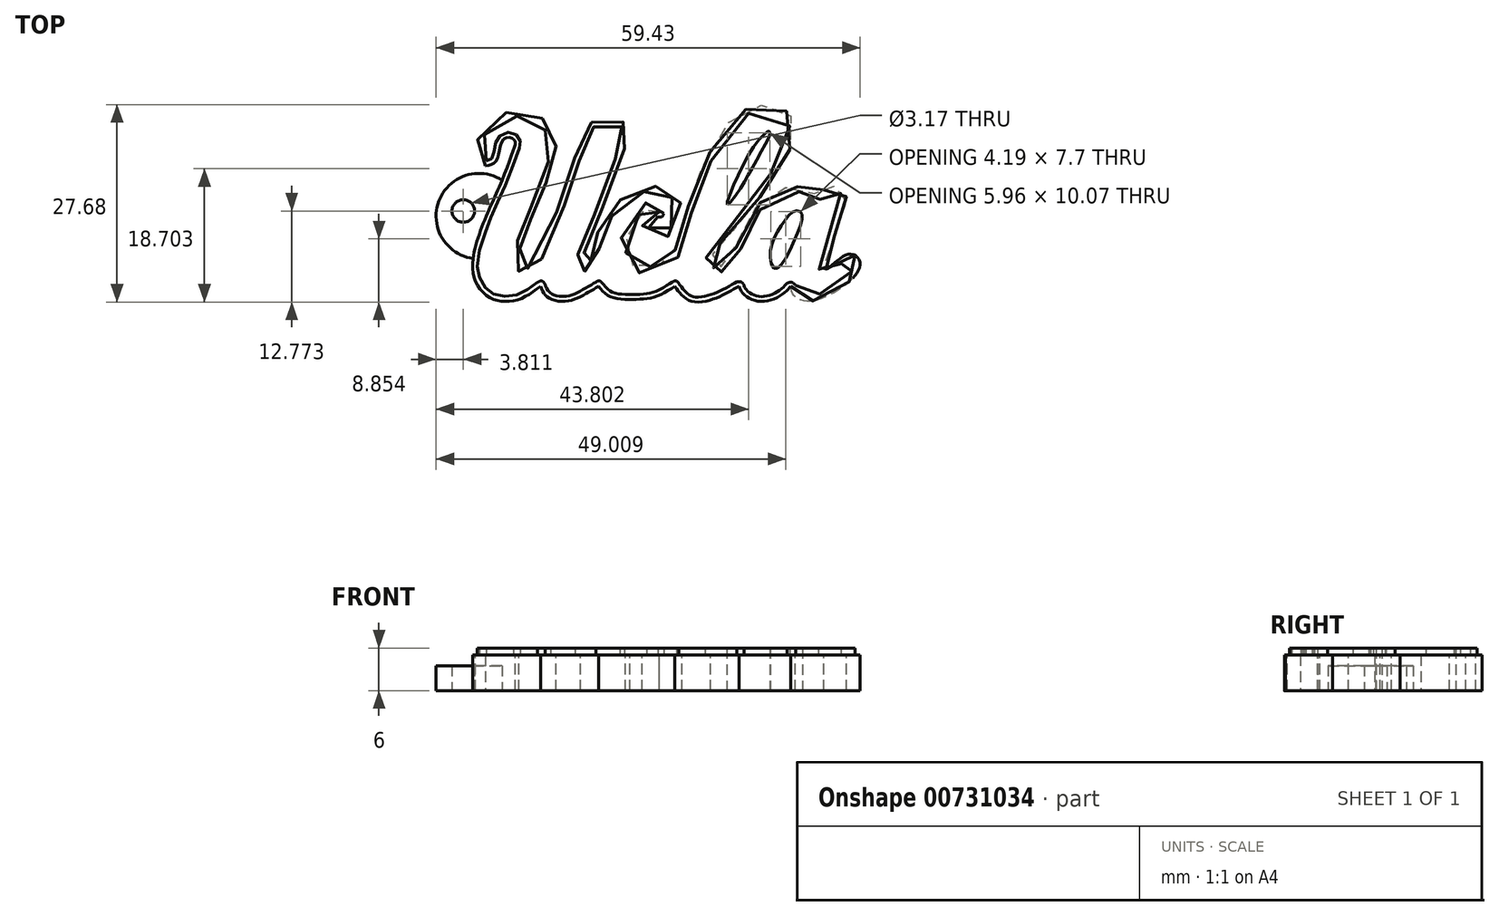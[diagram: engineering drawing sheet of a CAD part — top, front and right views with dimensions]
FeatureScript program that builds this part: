
annotation { "Feature Type Name" : "Feature", "Feature Type Description" : "" }
export const myFeature = defineFeature(function(context is Context, id is Id, definition is map)
    precondition{}
    {
        {
            var Q0;
            Q0=qCreatedBy(makeId("Top.planeOp"),FACE);
            var sketch = newSketch(context, id + "F0", { "sketchPlane" : qUnion([Q0])});
            skFitSpline(sketch, "E0", {"points": [v(-32.29, -2.1) * mm, v(-33.49, -1.15) * mm, v(-33.6, 0.71) * mm, v(-32.2, 3.77) * mm, v(-29.25, 5.4) * mm, v(-25.96, 5.38) * mm, v(-24.08, 4.39) * mm, v(-22.9, 2.53) * mm, v(-22.38, 0.67) * mm, v(-22.7, -1.4) * mm, v(-23.94, -4.94) * mm, v(-25.28, -8.23) * mm, v(-26.3, -10.38) * mm, v(-27.03, -12.53) * mm, v(-27.5, -13.99) * mm, v(-27.48, -15.85) * mm, v(-26.87, -16.53) * mm, v(-25.96, -16.2) * mm, v(-21.88, -7.39) * mm, v(-19.93, -1.51) * mm, v(-18.07, 3.2) * mm, v(-17.5, 3.93) * mm, v(-15.96, 4.16) * mm, v(-13.44, 4.16) * mm, v(-12.3, 3.64) * mm, v(-12.06, 2.82) * mm, v(-13.21, -0.8) * mm, v(-16.07, -8.52) * mm, v(-18.02, -13.37) * mm, v(-18.93, -15.64) * mm, v(-18.77, -16.2) * mm, v(-17.68, -15.6) * mm, v(-17.18, -14.6) * mm, v(-16.89, -12.63) * mm, v(-16.18, -10.6) * mm, v(-14.53, -7.95) * mm, v(-11.2, -5.41) * mm, v(-8.81, -4.94) * mm, v(-6.57, -5.32) * mm, v(-5.2, -6.7) * mm, v(-4.78, -8.93) * mm, v(-6.25, -11.76) * mm, v(-8.72, -12.13) * mm, v(-10, -11.15) * mm, v(-10.29, -9.56) * mm, v(-9.4, -8.47) * mm, v(-7.95, -8.57) * mm], "startDerivative": vector(-82.8, 46.2) * mm, "endDerivative": vector(90.83, -22.48) * mm});
            skFitSpline(sketch, "E1", {"points": [v(-7.95, -8.57) * mm, v(-7.95, -8.11) * mm, v(-8.83, -7.77) * mm, v(-10.4, -8.57) * mm, v(-11.92, -10.56) * mm, v(-12.67, -13.71) * mm, v(-12.03, -15.69) * mm, v(-10.74, -16.35) * mm, v(-8.52, -16.16) * mm, v(-6.7, -15.46) * mm, v(-5.84, -14.33) * mm, v(-5.27, -12.22) * mm, v(-3.9, -7.93) * mm, v(-2.26, -3.3) * mm, v(1.46, 3.6) * mm, v(4.6, 5.97) * mm, v(8.02, 6.43) * mm, v(10.24, 5.25) * mm, v(11.12, 2.73) * mm, v(10.04, -0.56) * mm, v(7.34, -4.94) * mm, v(2.14, -11.45) * mm, v(0, -13.65) * mm, v(-0.6, -14.96) * mm, v(-0.58, -16.28) * mm, v(0.49, -16.35) * mm, v(2.44, -15.42) * mm, v(2.96, -12.87) * mm, v(5.1, -8.57) * mm, v(8.24, -5.64) * mm, v(10.53, -5.05) * mm, v(13.28, -5.46) * mm, v(14.14, -6.2) * mm, v(15.12, -5.5) * mm, v(16.75, -4.98) * mm, v(18.02, -5.48) * mm, v(18.31, -6.68) * mm, v(17.9, -8.57) * mm, v(16.48, -12.2) * mm, v(15.23, -15.48) * mm, v(15.28, -16.55) * mm, v(16.48, -15.9) * mm, v(18.43, -14.55) * mm, v(19.83, -14.85) * mm, v(20.22, -16.14) * mm, v(19.18, -17.86) * mm, v(17.54, -19.27) * mm, v(14.4, -20.86) * mm, v(12.05, -20.97) * mm, v(10.88, -20.13) * mm, v(10.53, -19) * mm], "startDerivative": vector(14.19, 54.27) * mm, "endDerivative": vector(-13.26, 84.42) * mm});
            skFitSpline(sketch, "E2", {"points": [v(10.53, -19) * mm, v(9.7, -19.84) * mm, v(7.52, -20.97) * mm, v(5.05, -20.84) * mm, v(3.6, -19.7) * mm, v(3.28, -19) * mm], "startDerivative": vector(-4.2, -4.82) * mm, "endDerivative": vector(-1.54, 4.94) * mm});
            skFitSpline(sketch, "E3", {"points": [v(3.28, -19) * mm, v(1.6, -19.9) * mm, v(-0.58, -20.86) * mm, v(-3.23, -21.13) * mm, v(-4.78, -20.2) * mm, v(-5.73, -19) * mm], "startDerivative": vector(-8.47, -4.65) * mm, "endDerivative": vector(-5.03, 7.1) * mm});
            skFitSpline(sketch, "E4", {"points": [v(-5.73, -19) * mm, v(-8.74, -20.54) * mm, v(-11.67, -20.81) * mm, v(-14.7, -20.47) * mm, v(-16.43, -19) * mm], "startDerivative": vector(-11.13, -6.91) * mm, "endDerivative": vector(-6.78, 7.91) * mm});
            skFitSpline(sketch, "E5", {"points": [v(-16.43, -19) * mm, v(-18.52, -20.2) * mm, v(-21.15, -21.1) * mm, v(-23.7, -20.4) * mm, v(-24.55, -19) * mm], "startDerivative": vector(-7.97, -4.77) * mm, "endDerivative": vector(-2.84, 7.32) * mm});
            skFitSpline(sketch, "E6", {"points": [v(-24.55, -19) * mm, v(-27.1, -20.63) * mm, v(-29.57, -21.1) * mm, v(-31.9, -20.43) * mm, v(-33.67, -18.25) * mm, v(-34, -15.1) * mm, v(-32.24, -9.36) * mm, v(-29.94, -4.1) * mm, v(-28.27, 0.33) * mm, v(-28.1, 1.28) * mm, v(-28.73, 1.87) * mm, v(-29.86, 1.5) * mm, v(-30.45, -0.67) * mm, v(-31.18, -1.8) * mm, v(-32.29, -2.1) * mm], "startDerivative": vector(-31.72, -23.82) * mm, "endDerivative": vector(-24.62, -3.1) * mm});
            skFitSpline(sketch, "E7", {"points": [v(1.64, -7.53) * mm, v(2.2, -5.58) * mm, v(5.1, 0.21) * mm, v(7.17, 2.65) * mm, v(7.51, 2.77) * mm, v(7.6, 2.43) * mm, v(7.15, 1.33) * mm, v(5, -2.55) * mm, v(3.3, -5.52) * mm, v(1.64, -7.53) * mm]});
            skFitSpline(sketch, "E8", {"points": [v(11.84, -8.5) * mm, v(10.91, -8.5) * mm, v(9.6, -9.9) * mm, v(8.17, -12.27) * mm, v(7.65, -15.1) * mm, v(8.34, -16.53) * mm, v(9.82, -15.06) * mm, v(11.05, -12.48) * mm, v(12.15, -9.46) * mm, v(11.84, -8.5) * mm]});
            skArc(sketch, "E9", {"start": v(-29.94, -4.1) * mm, "mid": v(-38.81, -7.08) * mm, "end": v(-34, -15.1) * mm});
            skCircle(sketch, "E10", {"center": v(-35.37, -8.43) * mm, "radius": 1.59 * mm});
            skFitSpline(sketch, "E11.0", {"points": [v(-31.95, -1.49) * mm, v(-32.05, -1.43) * mm, v(-32.26, -1.31) * mm, v(-32.53, -1.15) * mm, v(-32.73, -1) * mm, v(-32.86, -0.85) * mm, v(-32.93, -0.72) * mm, v(-32.99, -0.53) * mm, v(-33.01, -0.27) * mm, v(-33, 0.06) * mm, v(-32.95, 0.44) * mm, v(-32.83, 1) * mm, v(-32.6, 1.76) * mm, v(-32.26, 2.49) * mm, v(-31.92, 3) * mm, v(-31.64, 3.36) * mm, v(-31.33, 3.66) * mm, v(-30.87, 4.03) * mm, v(-30.21, 4.4) * mm, v(-29.32, 4.7) * mm, v(-28.37, 4.86) * mm, v(-27.4, 4.9) * mm, v(-26.64, 4.81) * mm, v(-26.1, 4.7) * mm, v(-25.6, 4.56) * mm, v(-25.2, 4.37) * mm, v(-24.85, 4.14) * mm, v(-24.6, 3.93) * mm, v(-24.38, 3.7) * mm, v(-24.1, 3.32) * mm, v(-23.84, 2.88) * mm, v(-23.61, 2.42) * mm, v(-23.4, 1.94) * mm, v(-23.2, 1.38) * mm, v(-23.09, 0.85) * mm, v(-23.06, 0.46) * mm, v(-23.08, 0.04) * mm, v(-23.15, -0.41) * mm, v(-23.29, -0.93) * mm, v(-23.45, -1.5) * mm, v(-23.82, -2.61) * mm, v(-24.35, -4.04) * mm, v(-24.88, -5.45) * mm, v(-25.28, -6.46) * mm, v(-25.6, -7.24) * mm, v(-25.86, -7.8) * mm, v(-26.1, -8.34) * mm, v(-26.43, -8.98) * mm, v(-26.75, -9.63) * mm, v(-26.98, -10.2) * mm, v(-27.2, -10.77) * mm, v(-27.38, -11.34) * mm, v(-27.54, -11.87) * mm, v(-27.66, -12.24) * mm, v(-27.78, -12.55) * mm, v(-27.94, -12.98) * mm, v(-28.1, -13.44) * mm, v(-28.22, -13.99) * mm, v(-28.28, -14.44) * mm, v(-28.31, -14.9) * mm, v(-28.3, -15.37) * mm, v(-28.22, -15.84) * mm, v(-28.07, -16.3) * mm, v(-27.82, -16.7) * mm, v(-27.55, -16.95) * mm, v(-27.3, -17.1) * mm, v(-27.1, -17.2) * mm, v(-26.87, -17.26) * mm, v(-26.62, -17.28) * mm, v(-26.35, -17.25) * mm, v(-26, -17.14) * mm, v(-25.63, -16.9) * mm, v(-25.24, -16.47) * mm, v(-24.87, -15.93) * mm, v(-24.48, -15.29) * mm, v(-23.96, -14.3) * mm, v(-23.28, -12.85) * mm, v(-22.48, -10.95) * mm, v(-21.85, -9.35) * mm, v(-21.4, -8.14) * mm, v(-21, -7.02) * mm, v(-20.58, -5.78) * mm, v(-20.16, -4.48) * mm, v(-19.85, -3.48) * mm, v(-19.59, -2.68) * mm, v(-19.38, -2.07) * mm, v(-19.16, -1.44) * mm, v(-18.84, -0.56) * mm, v(-18.42, 0.55) * mm, v(-18.01, 1.58) * mm, v(-17.72, 2.27) * mm, v(-17.52, 2.71) * mm, v(-17.36, 3.06) * mm, v(-17.27, 3.22) * mm, v(-17.23, 3.27) * mm, v(-17.22, 3.29) * mm, v(-17.22, 3.3) * mm, v(-17.2, 3.3) * mm, v(-17.1, 3.34) * mm, v(-16.85, 3.39) * mm, v(-16.52, 3.42) * mm, v(-16.13, 3.45) * mm, v(-15.69, 3.47) * mm, v(-15.24, 3.5) * mm, v(-14.79, 3.52) * mm, v(-14.35, 3.53) * mm, v(-13.95, 3.52) * mm, v(-13.6, 3.48) * mm, v(-13.31, 3.42) * mm, v(-13.08, 3.34) * mm, v(-12.92, 3.25) * mm, v(-12.83, 3.18) * mm, v(-12.8, 3.14) * mm, v(-12.78, 3.11) * mm, v(-12.77, 3.08) * mm, v(-12.75, 2.97) * mm, v(-12.76, 2.75) * mm, v(-12.82, 2.42) * mm, v(-12.97, 1.87) * mm, v(-13.27, 1.01) * mm, v(-13.74, -0.23) * mm, v(-14.27, -1.64) * mm, v(-14.83, -3.14) * mm, v(-15.4, -4.7) * mm, v(-15.98, -6.27) * mm, v(-16.54, -7.78) * mm, v(-17.06, -9.18) * mm, v(-17.55, -10.45) * mm, v(-18.02, -11.61) * mm, v(-18.39, -12.49) * mm, v(-18.68, -13.13) * mm, v(-18.9, -13.6) * mm, v(-19.1, -14.05) * mm, v(-19.3, -14.48) * mm, v(-19.46, -14.9) * mm, v(-19.57, -15.25) * mm, v(-19.62, -15.54) * mm, v(-19.65, -15.76) * mm, v(-19.65, -15.99) * mm, v(-19.6, -16.24) * mm, v(-19.5, -16.5) * mm, v(-19.32, -16.7) * mm, v(-19.14, -16.82) * mm, v(-18.94, -16.9) * mm, v(-18.74, -16.92) * mm, v(-18.58, -16.91) * mm, v(-18.4, -16.88) * mm, v(-18.2, -16.81) * mm, v(-18, -16.7) * mm, v(-17.8, -16.59) * mm, v(-17.54, -16.41) * mm, v(-17.25, -16.17) * mm, v(-16.95, -15.84) * mm, v(-16.73, -15.49) * mm, v(-16.58, -15.11) * mm, v(-16.5, -14.75) * mm, v(-16.4, -14.24) * mm, v(-16.35, -13.7) * mm, v(-16.27, -13.17) * mm, v(-16.2, -12.79) * mm, v(-16.13, -12.44) * mm, v(-16, -11.97) * mm, v(-15.82, -11.5) * mm, v(-15.6, -11.02) * mm, v(-15.37, -10.5) * mm, v(-15.03, -9.85) * mm, v(-14.53, -9.06) * mm, v(-13.9, -8.27) * mm, v(-13.1, -7.5) * mm, v(-12.35, -6.9) * mm, v(-11.75, -6.5) * mm, v(-11.3, -6.24) * mm, v(-10.89, -6.04) * mm, v(-10.37, -5.83) * mm, v(-9.77, -5.69) * mm, v(-9.16, -5.64) * mm, v(-8.62, -5.63) * mm, v(-8.22, -5.65) * mm, v(-7.83, -5.68) * mm, v(-7.47, -5.74) * mm, v(-7.14, -5.84) * mm, v(-6.86, -5.95) * mm, v(-6.6, -6.1) * mm, v(-6.3, -6.35) * mm, v(-6.03, -6.67) * mm, v(-5.8, -7.06) * mm, v(-5.62, -7.46) * mm, v(-5.5, -7.88) * mm, v(-5.45, -8.35) * mm, v(-5.45, -8.72) * mm, v(-5.5, -9.13) * mm, v(-5.65, -9.7) * mm, v(-5.88, -10.28) * mm, v(-6.2, -10.75) * mm, v(-6.41, -11) * mm, v(-6.6, -11.15) * mm, v(-6.78, -11.28) * mm, v(-7.04, -11.4) * mm, v(-7.38, -11.5) * mm, v(-7.74, -11.55) * mm, v(-8.1, -11.54) * mm, v(-8.42, -11.49) * mm, v(-8.7, -11.4) * mm, v(-9, -11.25) * mm, v(-9.22, -11.05) * mm, v(-9.4, -10.78) * mm, v(-9.52, -10.54) * mm, v(-9.6, -10.29) * mm, v(-9.64, -10.04) * mm, v(-9.63, -9.8) * mm, v(-9.58, -9.61) * mm, v(-9.49, -9.42) * mm, v(-9.36, -9.26) * mm, v(-9.25, -9.18) * mm, v(-9.17, -9.14) * mm, v(-9.1, -9.11) * mm, v(-8.98, -9.1) * mm, v(-8.75, -9.1) * mm, v(-8.46, -9.16) * mm, v(-8.24, -9.22) * mm, v(-8.12, -9.24) * mm]});
            skFitSpline(sketch, "E12.0", {"points": [v(-7.27, -8.74) * mm, v(-7.26, -8.7) * mm, v(-7.24, -8.62) * mm, v(-7.2, -8.44) * mm, v(-7.2, -8.2) * mm, v(-7.25, -7.94) * mm, v(-7.35, -7.74) * mm, v(-7.48, -7.57) * mm, v(-7.65, -7.41) * mm, v(-7.87, -7.28) * mm, v(-8.1, -7.18) * mm, v(-8.35, -7.11) * mm, v(-8.6, -7.07) * mm, v(-8.88, -7.07) * mm, v(-9.24, -7.1) * mm, v(-9.66, -7.24) * mm, v(-10.12, -7.47) * mm, v(-10.53, -7.76) * mm, v(-10.91, -8.08) * mm, v(-11.28, -8.43) * mm, v(-11.74, -8.94) * mm, v(-12.16, -9.52) * mm, v(-12.52, -10.19) * mm, v(-12.85, -10.9) * mm, v(-13.17, -11.88) * mm, v(-13.35, -12.88) * mm, v(-13.38, -13.68) * mm, v(-13.33, -14.45) * mm, v(-13.15, -15.16) * mm, v(-12.84, -15.79) * mm, v(-12.53, -16.2) * mm, v(-12.16, -16.55) * mm, v(-11.58, -16.88) * mm, v(-10.78, -17.09) * mm, v(-9.77, -17.09) * mm, v(-8.76, -16.94) * mm, v(-7.96, -16.76) * mm, v(-7.34, -16.57) * mm, v(-6.9, -16.39) * mm, v(-6.47, -16.16) * mm, v(-6.08, -15.87) * mm, v(-5.75, -15.54) * mm, v(-5.38, -15.04) * mm, v(-5.07, -14.35) * mm, v(-4.9, -13.64) * mm, v(-4.76, -13.04) * mm, v(-4.64, -12.56) * mm, v(-4.5, -12.05) * mm, v(-4.28, -11.3) * mm, v(-3.95, -10.28) * mm, v(-3.59, -9.22) * mm, v(-3.3, -8.37) * mm, v(-3.03, -7.55) * mm, v(-2.7, -6.56) * mm, v(-2.3, -5.36) * mm, v(-1.9, -4.3) * mm, v(-1.53, -3.37) * mm, v(-1.1, -2.38) * mm, v(-0.5, -1.07) * mm, v(0.3, 0.5) * mm, v(1.15, 1.97) * mm, v(2.02, 3.21) * mm, v(2.84, 4.12) * mm, v(3.67, 4.77) * mm, v(4.54, 5.23) * mm, v(5.54, 5.57) * mm, v(6.6, 5.77) * mm, v(7.6, 5.8) * mm, v(8.46, 5.65) * mm, v(9.16, 5.31) * mm, v(9.73, 4.83) * mm, v(10.16, 4.16) * mm, v(10.37, 3.49) * mm, v(10.43, 2.93) * mm, v(10.42, 2.37) * mm, v(10.25, 1.6) * mm, v(9.85, 0.6) * mm, v(9.32, -0.44) * mm, v(8.74, -1.5) * mm, v(8.07, -2.6) * mm, v(7.43, -3.58) * mm, v(6.84, -4.44) * mm, v(6.2, -5.34) * mm, v(5.3, -6.55) * mm, v(4.17, -8) * mm, v(3.03, -9.4) * mm, v(2.14, -10.43) * mm, v(1.5, -11.12) * mm, v(0.9, -11.72) * mm, v(0.24, -12.35) * mm, v(-0.32, -12.9) * mm, v(-0.69, -13.4) * mm, v(-0.92, -13.77) * mm, v(-1.1, -14.16) * mm, v(-1.23, -14.58) * mm, v(-1.33, -15) * mm, v(-1.4, -15.4) * mm, v(-1.41, -15.73) * mm, v(-1.4, -15.98) * mm, v(-1.36, -16.24) * mm, v(-1.28, -16.48) * mm, v(-1.16, -16.68) * mm, v(-1, -16.87) * mm, v(-0.75, -17.03) * mm, v(-0.45, -17.12) * mm, v(-0.19, -17.14) * mm, v(0.06, -17.13) * mm, v(0.29, -17.1) * mm, v(0.52, -17.05) * mm, v(0.81, -17) * mm, v(1.22, -16.9) * mm, v(1.74, -16.72) * mm, v(2.17, -16.53) * mm, v(2.5, -16.32) * mm, v(2.73, -16.13) * mm, v(2.95, -15.91) * mm, v(3.13, -15.64) * mm, v(3.27, -15.37) * mm, v(3.39, -15) * mm, v(3.47, -14.55) * mm, v(3.52, -14.02) * mm, v(3.56, -13.6) * mm, v(3.6, -13.25) * mm, v(3.65, -13) * mm, v(3.7, -12.74) * mm, v(3.8, -12.39) * mm, v(3.95, -11.93) * mm, v(4.18, -11.37) * mm, v(4.56, -10.61) * mm, v(5.14, -9.67) * mm, v(5.94, -8.58) * mm, v(6.82, -7.62) * mm, v(7.7, -6.81) * mm, v(8.55, -6.24) * mm, v(9.14, -5.98) * mm, v(9.62, -5.86) * mm, v(10.01, -5.8) * mm, v(10.45, -5.75) * mm, v(10.95, -5.73) * mm, v(11.45, -5.73) * mm, v(11.95, -5.76) * mm, v(12.31, -5.82) * mm, v(12.56, -5.88) * mm, v(12.71, -5.94) * mm, v(12.84, -6) * mm, v(12.93, -6.06) * mm, v(13.02, -6.15) * mm, v(13.12, -6.25) * mm, v(13.23, -6.38) * mm, v(13.36, -6.52) * mm, v(13.5, -6.66) * mm, v(13.66, -6.77) * mm, v(13.82, -6.85) * mm, v(14.02, -6.9) * mm, v(14.24, -6.91) * mm, v(14.43, -6.87) * mm, v(14.63, -6.8) * mm, v(14.82, -6.68) * mm, v(15, -6.54) * mm, v(15.15, -6.4) * mm, v(15.3, -6.27) * mm, v(15.43, -6.15) * mm, v(15.55, -6.05) * mm, v(15.67, -5.97) * mm, v(15.84, -5.87) * mm, v(16.07, -5.78) * mm, v(16.36, -5.7) * mm, v(16.65, -5.67) * mm, v(16.93, -5.7) * mm, v(17.18, -5.75) * mm, v(17.35, -5.82) * mm, v(17.43, -5.88) * mm, v(17.48, -5.92) * mm, v(17.5, -5.96) * mm, v(17.54, -6.02) * mm, v(17.59, -6.15) * mm, v(17.62, -6.4) * mm, v(17.62, -6.69) * mm, v(17.59, -7) * mm, v(17.5, -7.46) * mm, v(17.33, -8.1) * mm, v(17, -9.07) * mm, v(16.57, -10.16) * mm, v(16.1, -11.32) * mm, v(15.68, -12.29) * mm, v(15.35, -13.04) * mm, v(15.12, -13.6) * mm, v(14.9, -14.15) * mm, v(14.72, -14.68) * mm, v(14.6, -15.11) * mm, v(14.52, -15.45) * mm, v(14.47, -15.7) * mm, v(14.44, -15.95) * mm, v(14.43, -16.2) * mm, v(14.45, -16.41) * mm, v(14.5, -16.6) * mm, v(14.55, -16.76) * mm, v(14.65, -16.92) * mm, v(14.8, -17.09) * mm, v(15.03, -17.22) * mm, v(15.25, -17.27) * mm, v(15.44, -17.27) * mm, v(15.65, -17.24) * mm, v(15.86, -17.16) * mm, v(16.08, -17.05) * mm, v(16.29, -16.92) * mm, v(16.5, -16.77) * mm, v(16.77, -16.56) * mm, v(17.1, -16.29) * mm, v(17.47, -15.96) * mm, v(17.83, -15.67) * mm, v(18.16, -15.43) * mm, v(18.4, -15.3) * mm, v(18.58, -15.24) * mm, v(18.73, -15.2) * mm, v(18.92, -15.19) * mm, v(19.12, -15.22) * mm, v(19.3, -15.3) * mm, v(19.4, -15.4) * mm, v(19.48, -15.52) * mm, v(19.54, -15.7) * mm, v(19.55, -15.9) * mm, v(19.52, -16.12) * mm, v(19.4, -16.4) * mm, v(19.22, -16.7) * mm, v(18.99, -17.02) * mm, v(18.72, -17.33) * mm, v(18.44, -17.63) * mm, v(18.08, -17.99) * mm, v(17.68, -18.32) * mm, v(17.2, -18.67) * mm, v(16.77, -18.94) * mm, v(16.32, -19.22) * mm, v(15.67, -19.58) * mm, v(14.99, -19.9) * mm, v(14.33, -20.15) * mm, v(13.72, -20.33) * mm, v(13.16, -20.4) * mm, v(12.68, -20.4) * mm, v(12.37, -20.34) * mm, v(12.09, -20.25) * mm, v(11.84, -20.12) * mm, v(11.64, -19.98) * mm, v(11.5, -19.82) * mm, v(11.4, -19.67) * mm, v(11.33, -19.46) * mm, v(11.28, -19.2) * mm, v(11.24, -19) * mm, v(11.23, -18.9) * mm]});
            skFitSpline(sketch, "E13.0", {"points": [v(10, -18.54) * mm, v(9.92, -18.64) * mm, v(9.75, -18.83) * mm, v(9.5, -19.1) * mm, v(9.16, -19.38) * mm, v(8.72, -19.69) * mm, v(8.2, -19.98) * mm, v(7.66, -20.21) * mm, v(7.1, -20.36) * mm, v(6.56, -20.42) * mm, v(6.02, -20.4) * mm, v(5.52, -20.28) * mm, v(5.08, -20.1) * mm, v(4.66, -19.82) * mm, v(4.39, -19.57) * mm, v(4.22, -19.38) * mm, v(4.14, -19.26) * mm, v(4.08, -19.16) * mm, v(4.02, -19.02) * mm, v(3.98, -18.9) * mm, v(3.95, -18.8) * mm]});
            skFitSpline(sketch, "E14.0", {"points": [v(2.94, -18.39) * mm, v(2.59, -18.58) * mm, v(2.06, -18.87) * mm, v(1.33, -19.26) * mm, v(0.77, -19.55) * mm, v(0.18, -19.83) * mm, v(-0.43, -20.08) * mm, v(-1.08, -20.29) * mm, v(-1.77, -20.44) * mm, v(-2.43, -20.52) * mm, v(-2.9, -20.49) * mm, v(-3.21, -20.42) * mm, v(-3.5, -20.31) * mm, v(-3.83, -20.12) * mm, v(-4.2, -19.8) * mm, v(-4.54, -19.43) * mm, v(-4.85, -19.03) * mm, v(-5.05, -18.74) * mm, v(-5.16, -18.6) * mm]});
            skFitSpline(sketch, "E15.0", {"points": [v(-6.1, -18.4) * mm, v(-6.56, -18.7) * mm, v(-7.24, -19.11) * mm, v(-8.11, -19.56) * mm, v(-8.75, -19.82) * mm, v(-9.35, -19.98) * mm, v(-9.99, -20.07) * mm, v(-10.67, -20.1) * mm, v(-11.4, -20.11) * mm, v(-12.18, -20.12) * mm, v(-12.93, -20.1) * mm, v(-13.63, -20.05) * mm, v(-14.24, -19.92) * mm, v(-14.68, -19.73) * mm, v(-15.09, -19.43) * mm, v(-15.49, -19.02) * mm, v(-15.76, -18.7) * mm, v(-15.9, -18.54) * mm]});
            skFitSpline(sketch, "E16.0", {"points": [v(-16.8, -18.4) * mm, v(-17.12, -18.6) * mm, v(-17.62, -18.9) * mm, v(-18.3, -19.28) * mm, v(-18.82, -19.57) * mm, v(-19.36, -19.85) * mm, v(-19.9, -20.1) * mm, v(-20.44, -20.29) * mm, v(-20.89, -20.38) * mm, v(-21.24, -20.42) * mm, v(-21.61, -20.42) * mm, v(-22.09, -20.37) * mm, v(-22.53, -20.24) * mm, v(-22.84, -20.12) * mm, v(-23.04, -20.01) * mm, v(-23.21, -19.9) * mm, v(-23.38, -19.75) * mm, v(-23.55, -19.53) * mm, v(-23.73, -19.18) * mm, v(-23.84, -18.9) * mm, v(-23.9, -18.75) * mm]});
            skFitSpline(sketch, "E17.0", {"points": [v(-24.97, -18.44) * mm, v(-25.3, -18.69) * mm, v(-25.95, -19.17) * mm, v(-26.74, -19.69) * mm, v(-27.36, -20) * mm, v(-27.98, -20.23) * mm, v(-28.6, -20.37) * mm, v(-29.24, -20.42) * mm, v(-29.89, -20.4) * mm, v(-30.5, -20.3) * mm, v(-31.07, -20.1) * mm, v(-31.47, -19.89) * mm, v(-31.84, -19.61) * mm, v(-32.32, -19.15) * mm, v(-32.73, -18.59) * mm, v(-33.04, -17.97) * mm, v(-33.2, -17.5) * mm, v(-33.32, -17.02) * mm, v(-33.4, -16.32) * mm, v(-33.36, -15.34) * mm, v(-33.08, -13.89) * mm, v(-32.6, -12.27) * mm, v(-32.1, -10.9) * mm, v(-31.68, -9.81) * mm, v(-31.24, -8.77) * mm, v(-30.69, -7.53) * mm, v(-30.02, -6.06) * mm, v(-29.35, -4.53) * mm, v(-28.81, -3.17) * mm, v(-28.42, -2.12) * mm, v(-28.15, -1.37) * mm, v(-27.9, -0.7) * mm, v(-27.73, -0.22) * mm, v(-27.61, 0.1) * mm, v(-27.53, 0.31) * mm, v(-27.46, 0.52) * mm, v(-27.4, 0.75) * mm, v(-27.36, 1) * mm, v(-27.37, 1.3) * mm, v(-27.45, 1.59) * mm, v(-27.58, 1.84) * mm, v(-27.76, 2.07) * mm, v(-27.97, 2.26) * mm, v(-28.22, 2.43) * mm, v(-28.51, 2.55) * mm, v(-28.83, 2.6) * mm, v(-29.25, 2.61) * mm, v(-29.67, 2.51) * mm, v(-30.07, 2.28) * mm, v(-30.29, 2.09) * mm, v(-30.44, 1.9) * mm, v(-30.58, 1.7) * mm, v(-30.7, 1.45) * mm, v(-30.8, 1.14) * mm, v(-30.9, 0.74) * mm, v(-30.99, 0.25) * mm, v(-31.06, -0.2) * mm, v(-31.12, -0.49) * mm, v(-31.2, -0.73) * mm, v(-31.3, -0.96) * mm, v(-31.4, -1.1) * mm, v(-31.5, -1.18) * mm, v(-31.56, -1.22) * mm, v(-31.63, -1.26) * mm, v(-31.77, -1.3) * mm, v(-32, -1.36) * mm, v(-32.25, -1.4) * mm, v(-32.37, -1.4) * mm]});
            skFitSpline(sketch, "E18", {"points": [v(-24.97, -18.44) * mm, v(-24.36, -18.25) * mm, v(-23.9, -18.75) * mm], "startDerivative": vector(1.33, 0.73) * mm, "endDerivative": vector(0.82, -1.34) * mm});
            skFitSpline(sketch, "E19", {"points": [v(-16.8, -18.4) * mm, v(-16.32, -18.2) * mm, v(-15.9, -18.54) * mm], "startDerivative": vector(0.99, 0.64) * mm, "endDerivative": vector(0.8, -0.92) * mm});
            skFitSpline(sketch, "E20", {"points": [v(-6.1, -18.4) * mm, v(-5.57, -18.2) * mm, v(-5.16, -18.6) * mm], "startDerivative": vector(1.1, 0.68) * mm, "endDerivative": vector(0.78, -1.06) * mm});
            skFitSpline(sketch, "E21", {"points": [v(2.94, -18.39) * mm, v(3.56, -18.39) * mm, v(3.95, -18.8) * mm], "startDerivative": vector(1.31, 0.21) * mm, "endDerivative": vector(0.7, -1.03) * mm});
            skFitSpline(sketch, "E22", {"points": [v(10, -18.54) * mm, v(10.67, -18.44) * mm, v(11.23, -18.9) * mm], "startDerivative": vector(1.42, 0.47) * mm, "endDerivative": vector(1.02, -1.17) * mm});
            skFitSpline(sketch, "E23", {"points": [v(-8.12, -9.24) * mm, v(-7.54, -9.24) * mm, v(-7.27, -8.74) * mm], "startDerivative": vector(1.3, -0.25) * mm, "endDerivative": vector(0.38, 1.26) * mm});
            skSolve(sketch);
        }
        {
            var Q0;
            Q0=makeQuery(id+"F0.imprint","IMPRINT",FACE,{"disambiguationData":[TD([[makeQuery(id+"F0.imprint","IMPRINT",EDGE,{"derivedFrom":sQuery(id+"F0.wireOp",EDGE,"E7")}),1.0]])]});
            extrude(context, id + "F1", {"entities" : qUnion([Q0]), "depth" : 6 * mm, "offsetDistance" : 25 * mm});
        }
        {
            var Q0;
            {var subQ0=sQuery(id+"F0.wireOp",EDGE,"E9");Q0=makeQuery(id+"F0.imprint","IMPRINT",FACE,{"disambiguationData":[TD([[makeQuery(id+"F0.imprint","IMPRINT",EDGE,{"derivedFrom":subQ0}),1.0]])]});}
            extrude(context, id + "F2", {"entities" : qUnion([Q0]), "operationType" : NewBodyOperationType.ADD, "depth" : 3.5 * mm, "offsetDistance" : 25 * mm});
        }
        {
            var Q0;
            {var subQ1=sQuery(id+"F0.wireOp",EDGE,"E0");Q0=makeQuery(id+"F0.imprint","IMPRINT",FACE,{"disambiguationData":[TD([[makeQuery(id+"F0.imprint","IMPRINT",EDGE,{"derivedFrom":subQ1}),-1.0]])]});}
            extrude(context, id + "F3", {"entities" : qUnion([Q0]), "operationType" : NewBodyOperationType.ADD, "depth" : 5 * mm, "offsetDistance" : 25 * mm});
        }
    });
